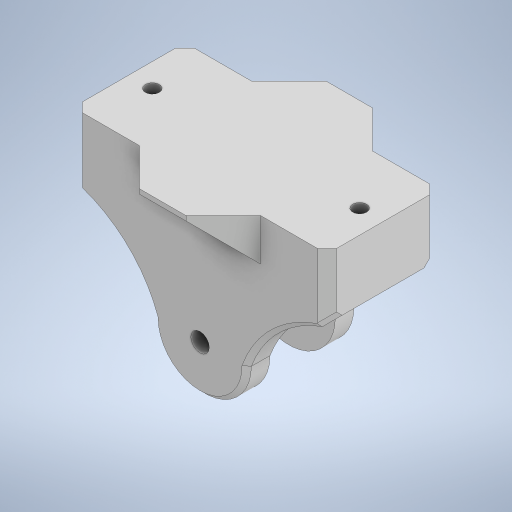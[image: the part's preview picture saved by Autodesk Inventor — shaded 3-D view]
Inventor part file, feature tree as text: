
AUTODESK INVENTOR PART (.ipt)
format: ipt  version: 2023.4 (Build 274418000, 418)  size: 382,976 bytes
history: native  units: mm
features: extrude x7, sketch x7, chamfer x5, plane x2, projected_geometry x2
ambient origin geometry x8: Origin, YZ Plane, XZ Plane, XY Plane, X Axis, Y Axis, Z Axis, Center Point
bodies: Solid1 (feature_tree)
feature tree (23):
  extrude  "Extrusion1"  Depth=60.0mm
  plane  "Work Plane1"
  extrude  "Extrusion2"  Depth=4.0mm
  chamfer  "Chamfer1"  Distance=48.0mm
  chamfer  "Chamfer2"  Distance=50.0mm
  extrude  "Extrusion3"  [1 undecoded]
  extrude  "Extrusion4"  Depth=10.0mm
  chamfer  "Chamfer3"  Distance=28.0mm
  extrude  "Extrusion5"  Depth=10.0mm TaperAngle=45.0deg
  plane  "Work Plane2"
  extrude  "Extrusion6"  Depth=10.0mm TaperAngle=45.0deg
  chamfer  "Chamfer4"  Distance=1.0mm
  extrude  "Extrusion7"  Depth=10.0mm TaperAngle=0.0deg
  chamfer  "Chamfer5"  Distance=2.0mm
  sketch  "Sketch1"  dims[d0=7.95mm d2=60.0mm]
  sketch  "Sketch2"  dims[d3=30.0mm d4=4.0mm]
  sketch  "Sketch3"  dims[d5=4.0mm]
  sketch  "Sketch4"  dims[d6=108.957421mm]
  projected_geometry  "Projected Loop1"
  sketch  "Sketch5"  dims[d7=30.0mm d8=48.0mm d9=0.0mm]
  projected_geometry  "Projected Loop2"
  sketch  "Sketch6"  dims[d10=40.0mm]
  sketch  "Sketch7"  dims[d11=50.0mm d12=50.0mm d13=-10.0mm d14=115.0mm d15=28.0mm d16=0.0mm d17=10.0mm d18=2.0mm d19=45.0deg d20=4.0mm d21=2.0mm d22=45.0deg d23=1.0mm d24=2.0mm d25=0.0mm d26=2.0mm d27=0.0mm d28=2.0mm d29=2.0mm d30=45.0deg d31=48.0mm d32=24.0mm d33=24.0mm d34=10.0mm d35=10.0mm d36=6.0mm d37=6.0mm d38=0.0mm d39=0.0mm d40=-16.0mm d41=14.0mm d42=14.0mm d43=0.0mm d44=0.0mm d45=2.0mm d46=2.0mm d47=45.0deg d48=16.0mm d49=16.0mm d50=100.957421mm d51=36.0mm d52=32.478711mm d53=10.0mm d54=0.0mm d55=8.0mm d56=2.0mm d57=45.0deg]
note: 1 required parameter value undecoded (feature->parameter linkage not recoverable at this tier; creation-order binding heuristic only, values carry confidence <= 0.55)
